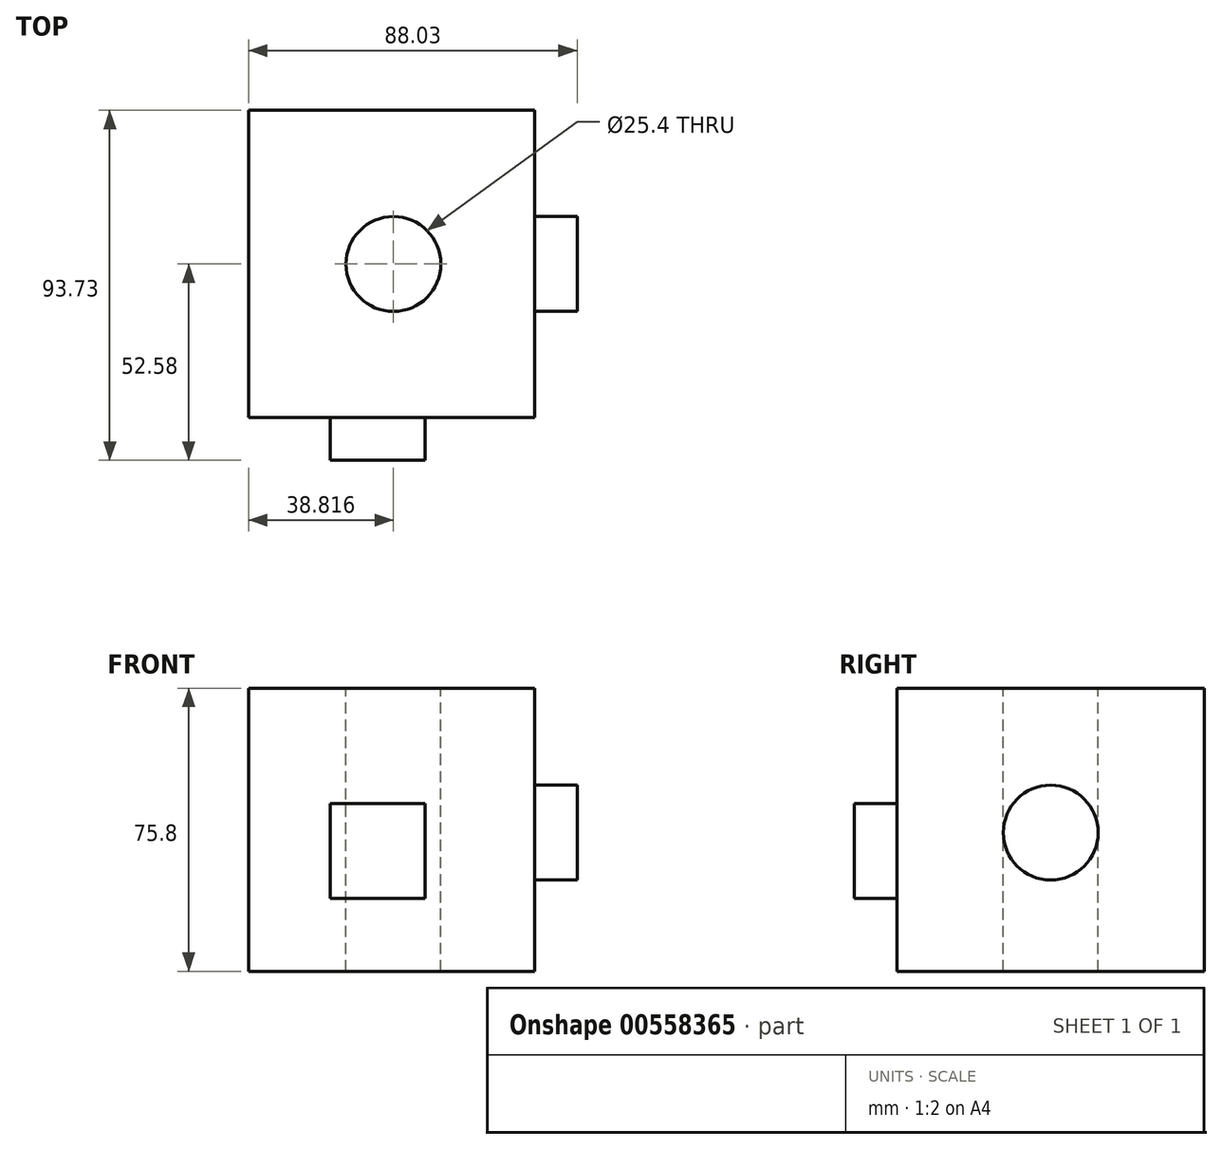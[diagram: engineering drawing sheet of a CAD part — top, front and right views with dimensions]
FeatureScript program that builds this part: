
annotation { "Feature Type Name" : "Feature", "Feature Type Description" : "" }
export const myFeature = defineFeature(function(context is Context, id is Id, definition is map)
    precondition{}
    {
        {
            var Q0;
            Q0=qCreatedBy(makeId("Front.planeOp"),FACE);
            var sketch = newSketch(context, id + "F0", { "sketchPlane" : qUnion([Q0])});
            skLineSegment(sketch, "E0.bottom", {"start": v(0, 0) * mm, "end": v(76.6, 0) * mm});
            skLineSegment(sketch, "E0.top", {"start": v(0, 75.8) * mm, "end": v(76.6, 75.8) * mm});
            skLineSegment(sketch, "E0.left", {"start": v(0, 0) * mm, "end": v(0, 75.8) * mm});
            skLineSegment(sketch, "E0.right", {"start": v(76.6, 0) * mm, "end": v(76.6, 75.8) * mm});
            skSolve(sketch);
        }
        {
            var Q0;
            Q0 = qSketchRegion(id + "F0", true);
            extrude(context, id + "F1", {"entities" : qUnion([Q0]), "endBound" : BoundingType.SYMMETRIC, "depth" : 82.3 * mm, "offsetDistance" : 25.4 * mm});
        }
        {
            var Q0;
            Q0=makeQuery(id+"F1.opExtrude","SWEPT_FACE",FACE,{"disambiguationData":[OSD([sQuery(id+"F0.wireOp",EDGE,"E0.top")])]});
            var sketch = newSketch(context, id + "F2", { "sketchPlane" : qUnion([Q0])});
            skPoint(sketch, "E1", {"position": v(38.82, 0) * mm});
            skSolve(sketch);
        }
        {
            var Q0;
            Q0=sQuery(id+"F2.wireOp",VERTEX,"E1");
            var Q1;
            Q1=makeQuery(id+"F1.opExtrude","SWEPT_BODY",BODY,{"disambiguationData":[OSD([sQuery(id+"F0.wireOp",EDGE,"E0.bottom"),sQuery(id+"F0.wireOp",EDGE,"E0.top"),sQuery(id+"F0.wireOp",EDGE,"E0.left"),sQuery(id+"F0.wireOp",EDGE,"E0.right")])]});
            hole(context, id + "F3", {"style" : HoleStyle.SIMPLE, "endStyle" : HoleEndStyle.THROUGH, "holeDiameter" : 25.4 * mm, "isTappedThrough" : true, "tappedDepth" : 12.7 * mm, "tapClearance" : 3, "locations" : qUnion([Q0]), "scope" : qUnion([Q1])});
        }
        {
            var Q0;
            Q0=makeQuery(id+"F1.opExtrude","CAP_FACE",FACE,{"disambiguationData":[OSD([sQuery(id+"F0.wireOp",EDGE,"E0.bottom"),sQuery(id+"F0.wireOp",EDGE,"E0.top"),sQuery(id+"F0.wireOp",EDGE,"E0.left"),sQuery(id+"F0.wireOp",EDGE,"E0.right")])],"isStart":false});
            var sketch = newSketch(context, id + "F4", { "sketchPlane" : qUnion([Q0])});
            skLineSegment(sketch, "E2.bottom", {"start": v(21.88, 44.92) * mm, "end": v(47.28, 44.92) * mm});
            skLineSegment(sketch, "E2.top", {"start": v(21.88, 19.52) * mm, "end": v(47.28, 19.52) * mm});
            skLineSegment(sketch, "E2.left", {"start": v(21.88, 44.92) * mm, "end": v(21.88, 19.52) * mm});
            skLineSegment(sketch, "E2.right", {"start": v(47.28, 44.92) * mm, "end": v(47.28, 19.52) * mm});
            skSolve(sketch);
        }
        {
            var Q0;
            Q0 = qSketchRegion(id + "F4", true);
            extrude(context, id + "F5", {"entities" : qUnion([Q0]), "operationType" : NewBodyOperationType.ADD, "depth" : 11.43 * mm, "offsetDistance" : 25.4 * mm});
        }
        {
            var Q0;
            Q0=makeQuery(id+"F1.opExtrude","SWEPT_FACE",FACE,{"disambiguationData":[OSD([sQuery(id+"F0.wireOp",EDGE,"E0.right")])]});
            var sketch = newSketch(context, id + "F6", { "sketchPlane" : qUnion([Q0])});
            skCircle(sketch, "E3", {"center": v(0, 37.12) * mm, "radius": 12.7 * mm});
            skSolve(sketch);
        }
        {
            var Q0;
            Q0 = qSketchRegion(id + "F6", true);
            extrude(context, id + "F7", {"entities" : qUnion([Q0]), "operationType" : NewBodyOperationType.ADD, "depth" : 11.43 * mm, "offsetDistance" : 25.4 * mm});
        }
    });
